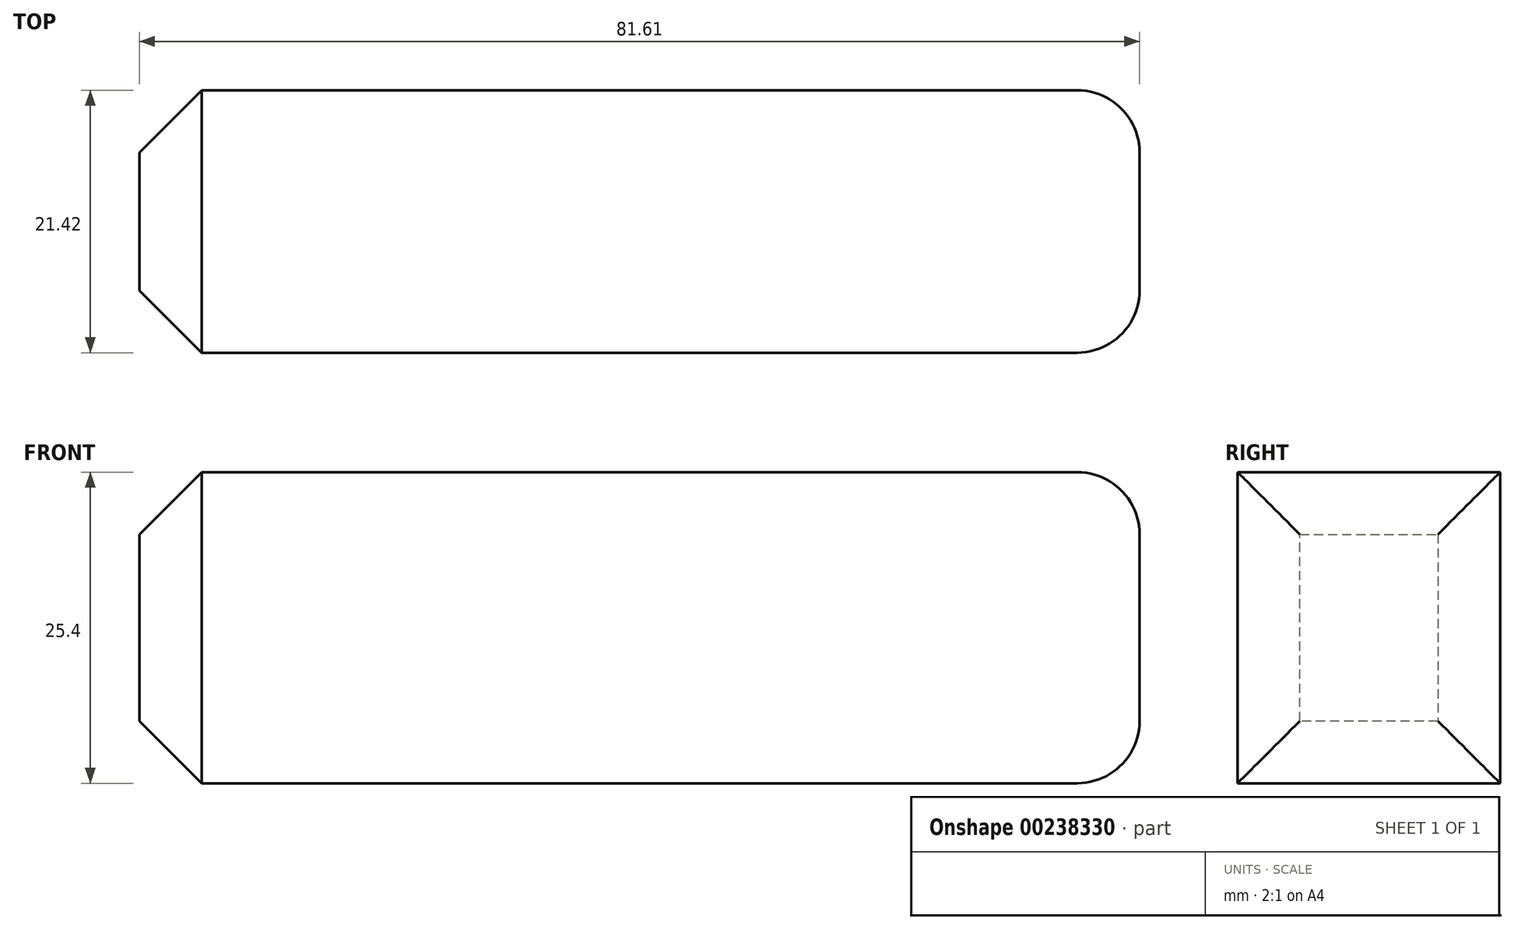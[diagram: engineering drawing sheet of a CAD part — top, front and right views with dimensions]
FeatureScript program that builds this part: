
annotation { "Feature Type Name" : "Feature", "Feature Type Description" : "" }
export const myFeature = defineFeature(function(context is Context, id is Id, definition is map)
    precondition{}
    {
        {
            var Q0;
            Q0=qCreatedBy(makeId("Top.planeOp"),FACE);
            var sketch = newSketch(context, id + "F0", { "sketchPlane" : qUnion([Q0])});
            skLineSegment(sketch, "E0.bottom", {"start": v(0, 0) * mm, "end": v(81.61, 0) * mm});
            skLineSegment(sketch, "E0.top", {"start": v(0, 21.42) * mm, "end": v(81.61, 21.42) * mm});
            skLineSegment(sketch, "E0.left", {"start": v(0, 0) * mm, "end": v(0, 21.42) * mm});
            skLineSegment(sketch, "E0.right", {"start": v(81.61, 0) * mm, "end": v(81.61, 21.42) * mm});
            skSolve(sketch);
        }
        {
            var Q0;
            Q0 = qSketchRegion(id + "F0", true);
            extrude(context, id + "F1", {"entities" : qUnion([Q0]), "depth" : 25.4 * mm});
        }
        {
            var Q0;
            Q0=makeQuery(id+"F1.opExtrude","CAP_EDGE",EDGE,{"disambiguationData":[OSD([sQuery(id+"F0.wireOp",EDGE,"E0.left")])],"isStart":false});
            var Q1;
            Q1=makeQuery(id+"F1.opExtrude","SWEPT_FACE",FACE,{"disambiguationData":[OSD([sQuery(id+"F0.wireOp",EDGE,"E0.left")])]});
            chamfer(context, id + "F2", {"entities" : qUnion([Q0, Q1]), "width" : 5.08 * mm, "tangentPropagation" : true});
        }
        {
            var Q0;
            Q0=makeQuery(id+"F1.opExtrude","SWEPT_FACE",FACE,{"disambiguationData":[OSD([sQuery(id+"F0.wireOp",EDGE,"E0.right")])]});
            fillet(context, id + "F3", {"entities" : qUnion([Q0]), "radius" : 5.08 * mm, "tangentPropagation" : true, "allowEdgeOverflow" : false});
        }
    });
